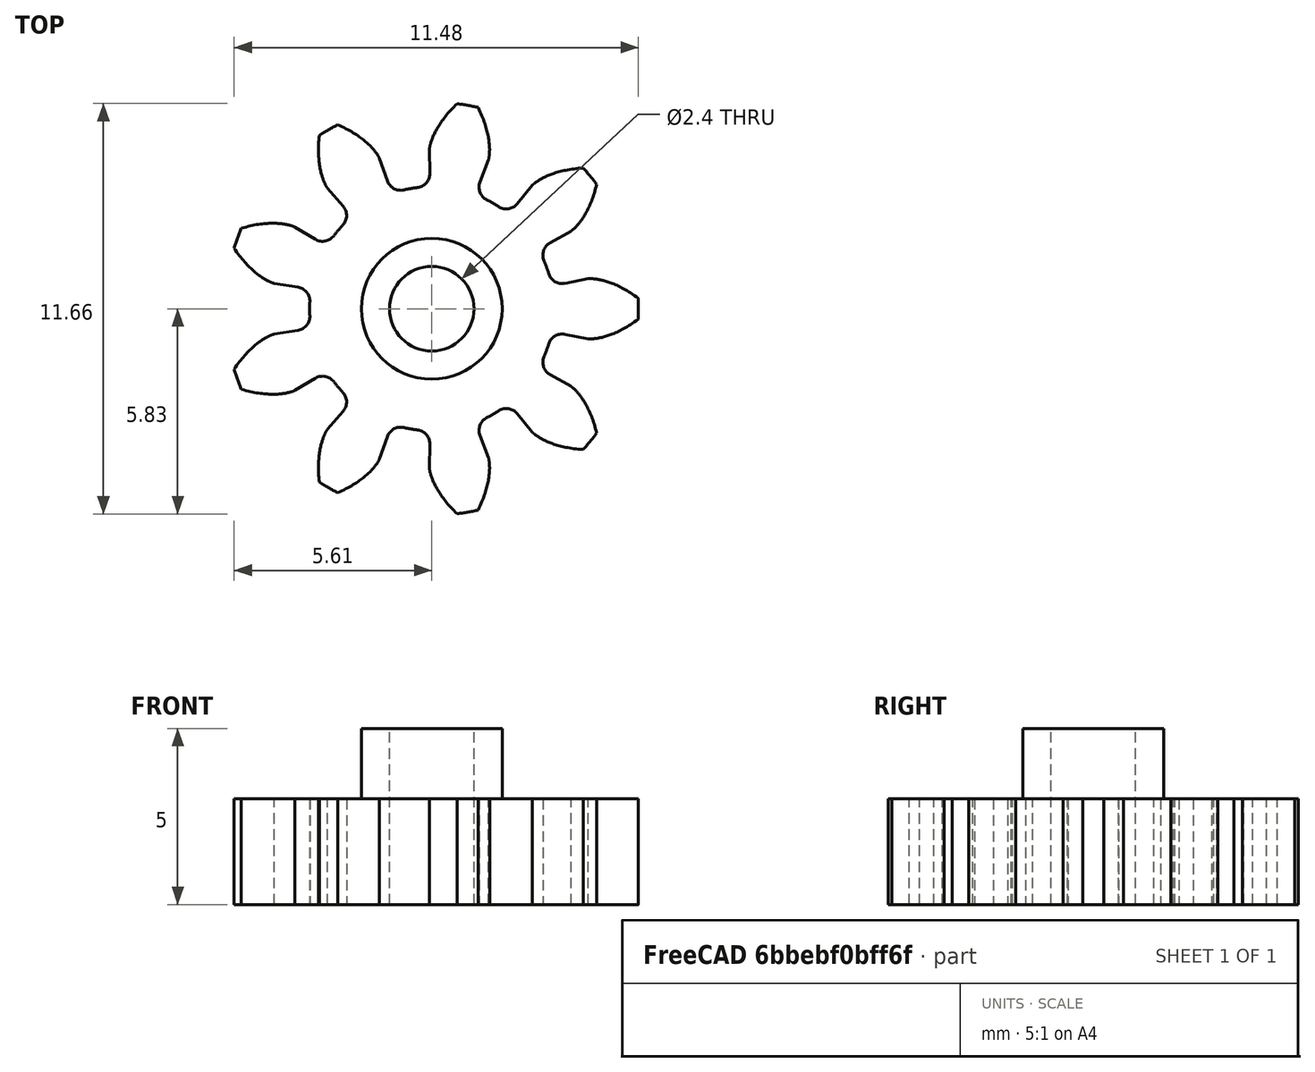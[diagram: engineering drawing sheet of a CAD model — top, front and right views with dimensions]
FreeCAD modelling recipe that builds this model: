
FCSTD DOCUMENT  (FreeCAD 0.17R13541 (Git))
Label: gear 9 inner shaft (new)
License: All rights reserved
LicenseURL: http://en.wikipedia.org/wiki/All_rights_reserved
objects: Part::Cylinder×3, Part::Cut×2, Part::Part2DObjectPython×1, Part::Extrusion×1, Part::MultiFuse×1
note: 8 computed .brp shape members not serialized (recipe doc carries the construction recipe); baked Part::Feature solids carry a one-line shape summary decoded from their .brp

FEATURE [Part::Part2DObjectPython] InvoluteGear  label="Engranaje 3 raw"  # Draft 2D object (typed FeaturePython)
  ExternalGear = true
  HighPrecision = true
  Modules = 1.067
  NumberOfTeeth = 9
  PressureAngle = 20
  expr: Modules = 1.0669999999999999
FEATURE [Part::Extrusion] Extrude  label="Engranaje 3 extruido"
  Base = -> InvoluteGear
  Dir = (0,0,1)
  DirMode = 2
  FaceMakerClass = Part::FaceMakerBullseye
  LengthFwd = 3
  LengthRev = 0
  Solid = true
  Symmetric = false
FEATURE [Part::Cylinder] Cylinder  label="Cilindro"
  Angle = 360
  AttacherType = Attacher::AttachEngine3D
  Height = 10
  Radius = 1.2
FEATURE [Part::Cut] Cut  label="Engranaje 3 agujereado"
  Base = -> Extrude
  Refine = true
  Tool = -> Cylinder
FEATURE [Part::Cylinder] Cylinder001  label="Cilindro exterior"
  Angle = 360
  AttacherType = Attacher::AttachEngine3D
  Height = 2
  Placement = pos=(0,0,3) rot=(0,0,1;0rad)
  Radius = 2
FEATURE [Part::Cylinder] Cylinder002  label="Cilindro interior"
  Angle = 360
  AttacherType = Attacher::AttachEngine3D
  Height = 10
  Placement = pos=(0,0,-2) rot=(0,0,1;0rad)
  Radius = 1.2
FEATURE [Part::MultiFuse] Fusion
  Refine = true
  Shapes = -> [Cut,Cylinder001]
FEATURE [Part::Cut] Cut001  label="Engranaje 3 final"
  Base = -> Fusion
  Refine = true
  Tool = -> Cylinder002
